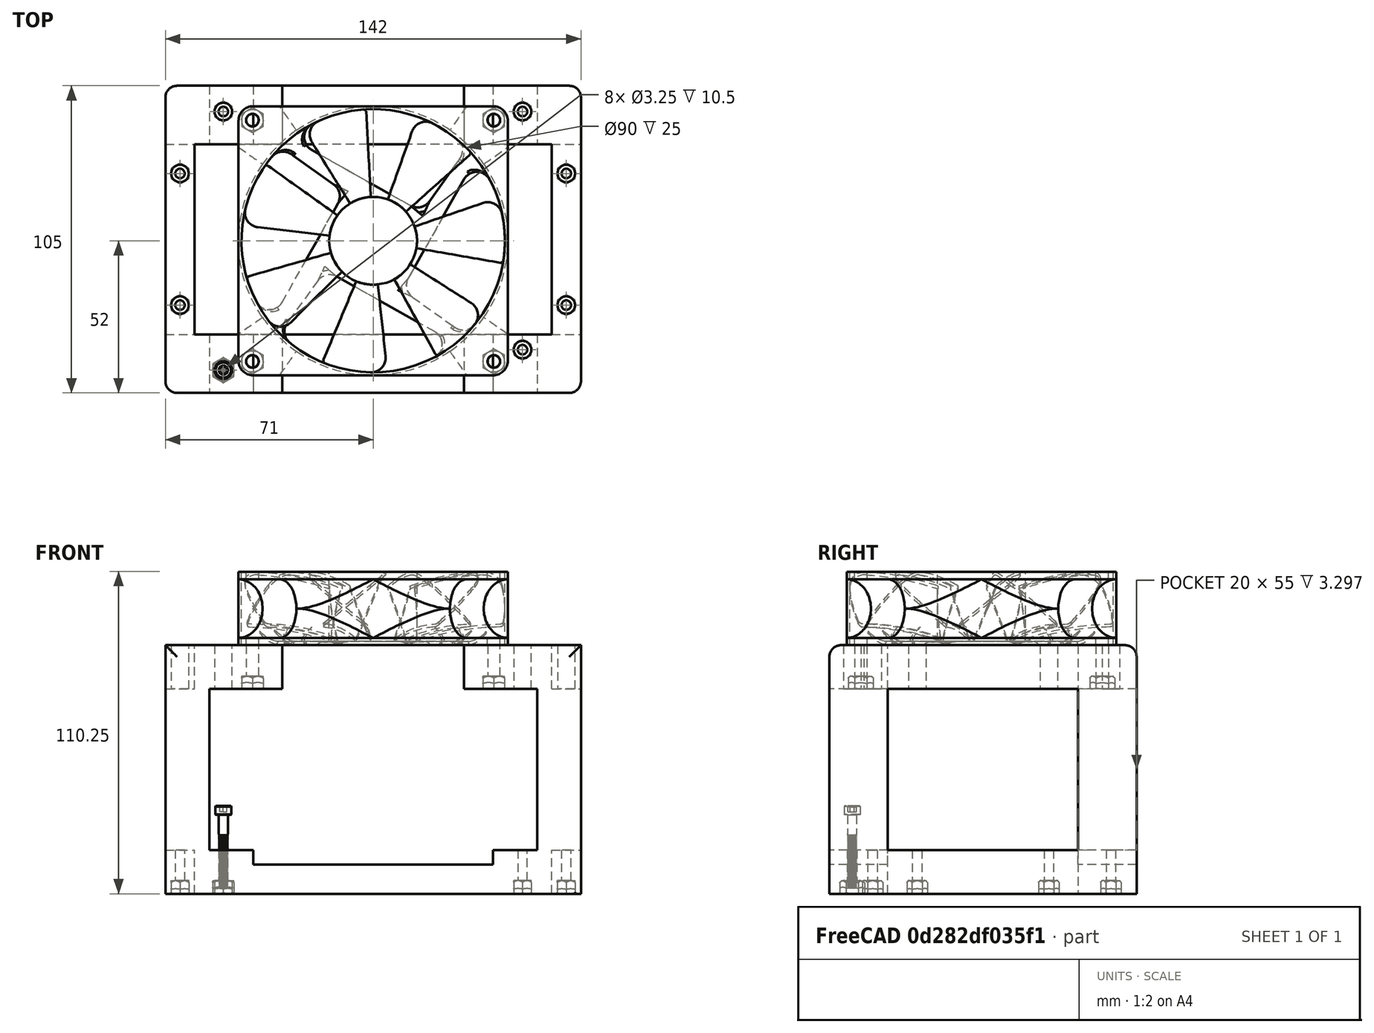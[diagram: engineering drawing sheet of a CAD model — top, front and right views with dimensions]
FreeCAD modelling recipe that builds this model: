
FCSTD DOCUMENT  (FreeCAD 0.20R29410 (Git))
Label: OdroidH4MountV3_2024_07_16
License: All rights reserved
LicenseURL: http://en.wikipedia.org/wiki/All_rights_reserved
objects: Part::MultiFuse×32, Part::FeaturePython×26, Part::Cylinder×13, Sketcher::SketchObject×10, Part::Extrusion×9, Part::Compound×5, Part::Feature×4, Mesh::Feature×1, Part::Cut×1, Part::Fillet×1, App::Part×1
note: 101 computed .brp shape members not serialized (recipe doc carries the construction recipe); baked Part::Feature solids carry a one-line shape summary decoded from their .brp

FEATURE [Mesh::Feature] Odroid_H004  label="Odroid-H004"
  Placement = pos=(16,0,25) rot=(0,0,1;0rad)
FEATURE [Part::Feature] Part__Feature002  label="fan form001"
  shape: bbox 105.3 x 105.3 x 25.46 mm, 118 faces (baked)
FEATURE [Part::Feature] Part__Feature003  label="fan001"
  Placement = pos=(0,0,1.25) rot=(0,0,-1;0.171016rad)
  shape: bbox 91.23 x 90.98 x 28.5 mm, 54 faces (baked)
FEATURE [Part::MultiFuse] Fusion  label="fan002"
  Placement = pos=(71,62,85) rot=(0,0,1;0rad)
  Shapes = -> [Part__Feature002,Part__Feature003]
FEATURE [Sketcher::SketchObject] Sketch006
  FullyConstrained = true
  Placement = pos=(0,0,0) rot=(0.57735,0.57735,0.57735;2.0944rad)
  sketch-geometry (8):
    g0: LineSegment StartX=30 StartY=15 StartZ=0 EndX=95 EndY=15 EndZ=0
    g1: LineSegment StartX=95 StartY=15 StartZ=0 EndX=95 EndY=0 EndZ=0
    g2: LineSegment StartX=95 StartY=0 StartZ=0 EndX=30 EndY=0 EndZ=0
    g3: LineSegment StartX=30 StartY=0 StartZ=0 EndX=30 EndY=15 EndZ=0
    g4: LineSegment StartX=30 StartY=85 StartZ=0 EndX=95 EndY=85 EndZ=0
    g5: LineSegment StartX=95 StartY=85 StartZ=0 EndX=95 EndY=70 EndZ=0
    g6: LineSegment StartX=95 StartY=70 StartZ=0 EndX=30 EndY=70 EndZ=0
    g7: LineSegment StartX=30 StartY=70 StartZ=0 EndX=30 EndY=85 EndZ=0
  constraints (24):
    c: Coincident(g0,g1)
    c: Coincident(g1,g2)
    c: Coincident(g2,g3)
    c: Coincident(g3,g0)
    c: Horizontal(g0)
    c: Horizontal(g2)
    c: Vertical(g1)
    c: Vertical(g3)
    c: PointOnObject(g1,g-1)
    c: Coincident(g4,g5)
    c: Coincident(g5,g6)
    c: Coincident(g6,g7)
    c: Coincident(g7,g4)
    c: Horizontal(g4)
    c: Horizontal(g6)
    c: Vertical(g5)
    c: Vertical(g7)
    c: DistanceX(g2) = 30
    c: DistanceY(g2,g0) = 15
    c: DistanceX(g0,g0) = 65
    c: DistanceY(g6,g4) = 15
    c: Vertical(g5,g0)
    c: Vertical(g6,g0)
    c: DistanceY(g0,g6) = 55
FEATURE [Sketcher::SketchObject] Sketch008
  FullyConstrained = true
  Placement = pos=(0,0,0) rot=(1,0,0;1.5708rad)
  sketch-geometry (16):
    g0: LineSegment StartX=0 StartY=0 StartZ=0 EndX=142 EndY=0 EndZ=0
    g1: LineSegment StartX=142 StartY=0 StartZ=0 EndX=142 EndY=85 EndZ=0
    g2: LineSegment StartX=142 StartY=85 StartZ=0 EndX=102 EndY=85 EndZ=0
    g3: LineSegment StartX=102 StartY=85 StartZ=0 EndX=102 EndY=70 EndZ=0
    g4: LineSegment StartX=102 StartY=70 StartZ=0 EndX=127 EndY=70 EndZ=0
    g5: LineSegment StartX=127 StartY=70 StartZ=0 EndX=127 EndY=15 EndZ=0
    g6: LineSegment StartX=127 StartY=15 StartZ=0 EndX=112 EndY=15 EndZ=0
    g7: LineSegment StartX=112 StartY=15 StartZ=0 EndX=112 EndY=10 EndZ=0
    g8: LineSegment StartX=112 StartY=10 StartZ=0 EndX=30 EndY=10 EndZ=0
    g9: LineSegment StartX=30 StartY=10 StartZ=0 EndX=30 EndY=15 EndZ=0
    g10: LineSegment StartX=30 StartY=15 StartZ=0 EndX=15 EndY=15 EndZ=0
    g11: LineSegment StartX=15 StartY=15 StartZ=0 EndX=15 EndY=70 EndZ=0
    g12: LineSegment StartX=15 StartY=70 StartZ=0 EndX=40 EndY=70 EndZ=0
    g13: LineSegment StartX=40 StartY=70 StartZ=0 EndX=40 EndY=85 EndZ=0
    g14: LineSegment StartX=40 StartY=85 StartZ=0 EndX=0 EndY=85 EndZ=0
    g15: LineSegment StartX=0 StartY=85 StartZ=0 EndX=0 EndY=0 EndZ=0
  constraints (47):
    c: Coincident(g0,g-1)
    c: Horizontal(g0)
    c: Coincident(g1,g0)
    c: Vertical(g1)
    c: Coincident(g2,g1)
    c: Horizontal(g2)
    c: Coincident(g3,g2)
    c: Vertical(g3)
    c: Coincident(g4,g3)
    c: Horizontal(g4)
    c: Coincident(g5,g4)
    c: Vertical(g5)
    c: Coincident(g6,g5)
    c: Horizontal(g6)
    c: Coincident(g7,g6)
    c: Coincident(g8,g7)
    c: Horizontal(g8)
    c: Coincident(g9,g8)
    c: Vertical(g9)
    c: Coincident(g10,g9)
    c: Horizontal(g10)
    c: Coincident(g11,g10)
    c: Vertical(g11)
    c: Coincident(g12,g11)
    c: Horizontal(g12)
    c: Coincident(g13,g12)
    c: Vertical(g13)
    c: Coincident(g14,g13)
    c: Horizontal(g14)
    c: Coincident(g15,g14)
    c: Coincident(g15,g0)
    c: Vertical(g15)
    c: DistanceX(g14,g14) = 40
    c: DistanceY(g0,g14) = 85
    c: DistanceX(g12,g12) = 25
    c: DistanceY(g12,g13) = 15
    c: DistanceY(g11,g11) = 55
    c: DistanceY(g9,g9) = 5
    c: DistanceX(g10,g10) = 15
    c: DistanceX(g8,g8) = 82
    c: DistanceY(g7,g7) = 5
    c: DistanceX(g6,g6) = 15
    c: DistanceY(g5,g5) = 55
    c: DistanceX(g4,g4) = 25
    c: DistanceX(g2,g2) = 40
    c: DistanceY(g3,g3) = 15
    c: DistanceX(g0,g0) = 142
FEATURE [Part::Extrusion] Extrude008
  Base = -> Sketch008
  Dir = (0,-1,-3e-16)
  DirMode = 2
  FaceMakerClass = Part::FaceMakerBullseye
  LengthFwd = 20
  LengthRev = 0
  Placement = pos=(0,30,0) rot=(0,0,1;0rad)
  Solid = true
  Symmetric = false
FEATURE [Sketcher::SketchObject] Sketch009
  FullyConstrained = true
  Placement = pos=(0,0,0) rot=(1,0,0;1.5708rad)
  sketch-geometry (16):
    g0: LineSegment StartX=0 StartY=0 StartZ=0 EndX=142 EndY=0 EndZ=0
    g1: LineSegment StartX=142 StartY=0 StartZ=0 EndX=142 EndY=85 EndZ=0
    g2: LineSegment StartX=142 StartY=85 StartZ=0 EndX=102 EndY=85 EndZ=0
    g3: LineSegment StartX=102 StartY=85 StartZ=0 EndX=102 EndY=70 EndZ=0
    g4: LineSegment StartX=102 StartY=70 StartZ=0 EndX=127 EndY=70 EndZ=0
    g5: LineSegment StartX=127 StartY=70 StartZ=0 EndX=127 EndY=15 EndZ=0
    g6: LineSegment StartX=127 StartY=15 StartZ=0 EndX=112 EndY=15 EndZ=0
    g7: LineSegment StartX=112 StartY=15 StartZ=0 EndX=112 EndY=10 EndZ=0
    g8: LineSegment StartX=112 StartY=10 StartZ=0 EndX=30 EndY=10 EndZ=0
    g9: LineSegment StartX=30 StartY=10 StartZ=0 EndX=30 EndY=15 EndZ=0
    g10: LineSegment StartX=30 StartY=15 StartZ=0 EndX=15 EndY=15 EndZ=0
    g11: LineSegment StartX=15 StartY=15 StartZ=0 EndX=15 EndY=70 EndZ=0
    g12: LineSegment StartX=15 StartY=70 StartZ=0 EndX=40 EndY=70 EndZ=0
    g13: LineSegment StartX=40 StartY=70 StartZ=0 EndX=40 EndY=85 EndZ=0
    g14: LineSegment StartX=40 StartY=85 StartZ=0 EndX=0 EndY=85 EndZ=0
    g15: LineSegment StartX=0 StartY=85 StartZ=0 EndX=0 EndY=0 EndZ=0
  constraints (47):
    c: Coincident(g0,g-1)
    c: Horizontal(g0)
    c: Coincident(g1,g0)
    c: Vertical(g1)
    c: Coincident(g2,g1)
    c: Horizontal(g2)
    c: Coincident(g3,g2)
    c: Vertical(g3)
    c: Coincident(g4,g3)
    c: Horizontal(g4)
    c: Coincident(g5,g4)
    c: Vertical(g5)
    c: Coincident(g6,g5)
    c: Horizontal(g6)
    c: Coincident(g7,g6)
    c: Coincident(g8,g7)
    c: Horizontal(g8)
    c: Coincident(g9,g8)
    c: Vertical(g9)
    c: Coincident(g10,g9)
    c: Horizontal(g10)
    c: Coincident(g11,g10)
    c: Vertical(g11)
    c: Coincident(g12,g11)
    c: Horizontal(g12)
    c: Coincident(g13,g12)
    c: Vertical(g13)
    c: Coincident(g14,g13)
    c: Horizontal(g14)
    c: Coincident(g15,g14)
    c: Coincident(g15,g0)
    c: Vertical(g15)
    c: DistanceX(g14,g14) = 40
    c: DistanceY(g0,g14) = 85
    c: DistanceX(g12,g12) = 25
    c: DistanceY(g12,g13) = 15
    c: DistanceY(g11,g11) = 55
    c: DistanceY(g9,g9) = 5
    c: DistanceX(g10,g10) = 15
    c: DistanceX(g8,g8) = 82
    c: DistanceY(g7,g7) = 5
    c: DistanceX(g6,g6) = 15
    c: DistanceY(g5,g5) = 55
    c: DistanceX(g4,g4) = 25
    c: DistanceX(g2,g2) = 40
    c: DistanceY(g3,g3) = 15
    c: DistanceX(g0,g0) = 142
FEATURE [Part::Extrusion] Extrude009
  Base = -> Sketch009
  Dir = (0,-1,-3e-16)
  DirMode = 2
  FaceMakerClass = Part::FaceMakerBullseye
  LengthFwd = 20
  LengthRev = 0
  Placement = pos=(0,115,0) rot=(0,0,1;0rad)
  Solid = true
  Symmetric = false
FEATURE [Sketcher::SketchObject] Sketch010
  FullyConstrained = true
  Placement = pos=(0,0,0) rot=(0.57735,0.57735,0.57735;2.0944rad)
  sketch-geometry (8):
    g0: LineSegment StartX=30 StartY=15 StartZ=0 EndX=95 EndY=15 EndZ=0
    g1: LineSegment StartX=95 StartY=15 StartZ=0 EndX=95 EndY=0 EndZ=0
    g2: LineSegment StartX=95 StartY=0 StartZ=0 EndX=30 EndY=0 EndZ=0
    g3: LineSegment StartX=30 StartY=0 StartZ=0 EndX=30 EndY=15 EndZ=0
    g4: LineSegment StartX=30 StartY=85 StartZ=0 EndX=95 EndY=85 EndZ=0
    g5: LineSegment StartX=95 StartY=85 StartZ=0 EndX=95 EndY=70 EndZ=0
    g6: LineSegment StartX=95 StartY=70 StartZ=0 EndX=30 EndY=70 EndZ=0
    g7: LineSegment StartX=30 StartY=70 StartZ=0 EndX=30 EndY=85 EndZ=0
  constraints (24):
    c: Coincident(g0,g1)
    c: Coincident(g1,g2)
    c: Coincident(g2,g3)
    c: Coincident(g3,g0)
    c: Horizontal(g0)
    c: Horizontal(g2)
    c: Vertical(g1)
    c: Vertical(g3)
    c: PointOnObject(g1,g-1)
    c: Coincident(g4,g5)
    c: Coincident(g5,g6)
    c: Coincident(g6,g7)
    c: Coincident(g7,g4)
    c: Horizontal(g4)
    c: Horizontal(g6)
    c: Vertical(g5)
    c: Vertical(g7)
    c: DistanceX(g2) = 30
    c: DistanceY(g2,g0) = 15
    c: DistanceX(g0,g0) = 65
    c: DistanceY(g6,g4) = 15
    c: Vertical(g5,g0)
    c: Vertical(g6,g0)
    c: DistanceY(g0,g6) = 55
FEATURE [Part::Extrusion] Extrude010
  Base = -> Sketch010
  Dir = (1,0,0)
  DirMode = 2
  FaceMakerClass = Part::FaceMakerBullseye
  LengthFwd = 10
  LengthRev = 0
  Solid = true
  Symmetric = false
FEATURE [Sketcher::SketchObject] Sketch011
  FullyConstrained = true
  Placement = pos=(0,0,0) rot=(0.57735,0.57735,0.57735;2.0944rad)
  sketch-geometry (8):
    g0: LineSegment StartX=30 StartY=15 StartZ=0 EndX=95 EndY=15 EndZ=0
    g1: LineSegment StartX=95 StartY=15 StartZ=0 EndX=95 EndY=0 EndZ=0
    g2: LineSegment StartX=95 StartY=0 StartZ=0 EndX=30 EndY=0 EndZ=0
    g3: LineSegment StartX=30 StartY=0 StartZ=0 EndX=30 EndY=15 EndZ=0
    g4: LineSegment StartX=30 StartY=85 StartZ=0 EndX=95 EndY=85 EndZ=0
    g5: LineSegment StartX=95 StartY=85 StartZ=0 EndX=95 EndY=70 EndZ=0
    g6: LineSegment StartX=95 StartY=70 StartZ=0 EndX=30 EndY=70 EndZ=0
    g7: LineSegment StartX=30 StartY=70 StartZ=0 EndX=30 EndY=85 EndZ=0
  constraints (24):
    c: Coincident(g0,g1)
    c: Coincident(g1,g2)
    c: Coincident(g2,g3)
    c: Coincident(g3,g0)
    c: Horizontal(g0)
    c: Horizontal(g2)
    c: Vertical(g1)
    c: Vertical(g3)
    c: PointOnObject(g1,g-1)
    c: Coincident(g4,g5)
    c: Coincident(g5,g6)
    c: Coincident(g6,g7)
    c: Coincident(g7,g4)
    c: Horizontal(g4)
    c: Horizontal(g6)
    c: Vertical(g5)
    c: Vertical(g7)
    c: DistanceX(g2) = 30
    c: DistanceY(g2,g0) = 15
    c: DistanceX(g0,g0) = 65
    c: DistanceY(g6,g4) = 15
    c: Vertical(g5,g0)
    c: Vertical(g6,g0)
    c: DistanceY(g0,g6) = 55
FEATURE [Part::Extrusion] Extrude011
  Base = -> Sketch011
  Dir = (1,0,0)
  DirMode = 2
  FaceMakerClass = Part::FaceMakerBullseye
  LengthFwd = 10
  LengthRev = 0
  Placement = pos=(132,0,0) rot=(0,0,1;0rad)
  Solid = true
  Symmetric = false
FEATURE [Part::MultiFuse] Fusion002
  Shapes = -> [Extrude011,Extrude008,Extrude009,Extrude010]
FEATURE [Sketcher::SketchObject] Sketch
  FullyConstrained = true
  sketch-geometry (4):
    g0: Circle CenterX=19.81 CenterY=106.19 CenterZ=0 NormalX=0 NormalY=0 NormalZ=1 AngleXU=0 Radius=1.625
    g1: Circle CenterX=122.04 CenterY=106.19 CenterZ=0 NormalX=0 NormalY=0 NormalZ=1 AngleXU=0 Radius=1.625
    g2: Circle CenterX=19.81 CenterY=17.78 CenterZ=0 NormalX=0 NormalY=0 NormalZ=1 AngleXU=0 Radius=1.625
    g3: Circle CenterX=122.04 CenterY=24.77 CenterZ=0 NormalX=0 NormalY=0 NormalZ=1 AngleXU=0 Radius=1.625
  constraints (12):
    c: Vertical(g0,g2)
    c: DistanceY(g2,g0) = 88.41
    c: DistanceX(g2) = 19.81
    c: DistanceY(g2) = 17.78
    c: DistanceX(g2,g3) = 102.23
    c: DistanceY(g2,g3) = 6.99
    c: DistanceX(g1,g3) = 0
    c: DistanceY(g0,g1) = 0
    c: Equal(g2,g3)
    c: Equal(g2,g1)
    c: Equal(g2,g0)
    c: Diameter(g2) = 3.25
FEATURE [Sketcher::SketchObject] Sketch012
  FullyConstrained = true
  sketch-geometry (4):
    g0: Circle CenterX=29.75 CenterY=103.25 CenterZ=0 NormalX=0 NormalY=0 NormalZ=1 AngleXU=0 Radius=2.125
    g1: Circle CenterX=112.25 CenterY=103.25 CenterZ=0 NormalX=0 NormalY=0 NormalZ=1 AngleXU=0 Radius=2.125
    g2: Circle CenterX=29.75 CenterY=20.75 CenterZ=0 NormalX=0 NormalY=0 NormalZ=1 AngleXU=0 Radius=2.125
    g3: Circle CenterX=112.25 CenterY=20.75 CenterZ=0 NormalX=0 NormalY=0 NormalZ=1 AngleXU=0 Radius=2.125
  constraints (12):
    c: Vertical(g0,g2)
    c: DistanceX(g1,g3) = 0
    c: DistanceY(g0,g1) = 0
    c: Equal(g2,g3)
    c: Equal(g2,g1)
    c: Equal(g2,g0)
    c: Diameter(g2) = 4.25
    c: DistanceX(g2) = 29.75
    c: DistanceY(g2) = 20.75
    c: Horizontal(g3,g2)
    c: DistanceX(g2,g3) = 82.5
    c: DistanceY(g2,g0) = 82.5
FEATURE [Part::Extrusion] Extrude
  Base = -> Sketch
  Dir = (0,0,1)
  DirMode = 2
  FaceMakerClass = Part::FaceMakerBullseye
  LengthFwd = 15
  LengthRev = 0
  Solid = true
  Symmetric = false
FEATURE [Part::Extrusion] Extrude012
  Base = -> Sketch012
  Dir = (0,0,1)
  DirMode = 2
  FaceMakerClass = Part::FaceMakerBullseye
  LengthFwd = 15
  LengthRev = 0
  Placement = pos=(0,0,70) rot=(0,0,1;0rad)
  Solid = true
  Symmetric = false
FEATURE [Sketcher::SketchObject] Sketch013
  FullyConstrained = true
  sketch-geometry (4):
    g0: Circle CenterX=19.81 CenterY=106.19 CenterZ=0 NormalX=0 NormalY=0 NormalZ=1 AngleXU=0 Radius=3
    g1: Circle CenterX=122.04 CenterY=106.19 CenterZ=0 NormalX=0 NormalY=0 NormalZ=1 AngleXU=0 Radius=3
    g2: Circle CenterX=19.81 CenterY=17.78 CenterZ=0 NormalX=0 NormalY=0 NormalZ=1 AngleXU=0 Radius=3
    g3: Circle CenterX=122.04 CenterY=24.77 CenterZ=0 NormalX=0 NormalY=0 NormalZ=1 AngleXU=0 Radius=3
  constraints (12):
    c: Vertical(g0,g2)
    c: DistanceY(g2,g0) = 88.41
    c: DistanceX(g2) = 19.81
    c: DistanceY(g2) = 17.78
    c: DistanceX(g2,g3) = 102.23
    c: DistanceY(g2,g3) = 6.99
    c: DistanceX(g1,g3) = 0
    c: DistanceY(g0,g1) = 0
    c: Equal(g2,g3)
    c: Equal(g2,g1)
    c: Equal(g2,g0)
    c: Diameter(g2) = 6
FEATURE [Part::Extrusion] Extrude013
  Base = -> Sketch013
  Dir = (0,0,1)
  DirMode = 2
  FaceMakerClass = Part::FaceMakerBullseye
  LengthFwd = 15
  LengthRev = 0
  Placement = pos=(0,0,70) rot=(0,0,1;0rad)
  Solid = true
  Symmetric = false
FEATURE [Sketcher::SketchObject] Sketch014
  FullyConstrained = true
  sketch-geometry (4):
    g0: Circle CenterX=5 CenterY=85 CenterZ=0 NormalX=0 NormalY=0 NormalZ=1 AngleXU=0 Radius=1.625
    g1: Circle CenterX=137 CenterY=85 CenterZ=0 NormalX=0 NormalY=0 NormalZ=1 AngleXU=0 Radius=1.625
    g2: Circle CenterX=5 CenterY=40 CenterZ=0 NormalX=0 NormalY=0 NormalZ=1 AngleXU=0 Radius=1.625
    g3: Circle CenterX=137 CenterY=40 CenterZ=0 NormalX=0 NormalY=0 NormalZ=1 AngleXU=0 Radius=1.625
  constraints (12):
    c: Vertical(g0,g2)
    c: DistanceY(g2,g0) = 45
    c: DistanceX(g2,g3) = 132
    c: DistanceY(g2,g3) = 0
    c: DistanceX(g1,g3) = 0
    c: DistanceY(g0,g1) = 0
    c: Equal(g2,g3)
    c: Equal(g2,g1)
    c: Equal(g2,g0)
    c: Diameter(g2) = 3.25
    c: DistanceX(g2) = 5
    c: DistanceY(g2) = 40
FEATURE [Sketcher::SketchObject] Sketch015
  FullyConstrained = true
  sketch-geometry (4):
    g0: Circle CenterX=5 CenterY=85 CenterZ=0 NormalX=0 NormalY=0 NormalZ=1 AngleXU=0 Radius=3
    g1: Circle CenterX=137 CenterY=85 CenterZ=0 NormalX=0 NormalY=0 NormalZ=1 AngleXU=0 Radius=3
    g2: Circle CenterX=5 CenterY=40 CenterZ=0 NormalX=0 NormalY=0 NormalZ=1 AngleXU=0 Radius=3
    g3: Circle CenterX=137 CenterY=40 CenterZ=0 NormalX=0 NormalY=0 NormalZ=1 AngleXU=0 Radius=3
  constraints (12):
    c: Vertical(g0,g2)
    c: DistanceY(g2,g0) = 45
    c: DistanceX(g2,g3) = 132
    c: DistanceY(g2,g3) = 0
    c: DistanceX(g1,g3) = 0
    c: DistanceY(g0,g1) = 0
    c: Equal(g2,g3)
    c: Equal(g2,g1)
    c: Equal(g2,g0)
    c: Diameter(g2) = 6
    c: DistanceX(g2) = 5
    c: DistanceY(g2) = 40
FEATURE [Part::Extrusion] Extrude014
  Base = -> Sketch014
  Dir = (0,0,1)
  DirMode = 2
  FaceMakerClass = Part::FaceMakerBullseye
  LengthFwd = 15
  LengthRev = 0
  Solid = true
  Symmetric = false
FEATURE [Part::Extrusion] Extrude015
  Base = -> Sketch015
  Dir = (0,0,1)
  DirMode = 2
  FaceMakerClass = Part::FaceMakerBullseye
  LengthFwd = 15
  LengthRev = 0
  Placement = pos=(0,0,70) rot=(0,0,1;0rad)
  Solid = true
  Symmetric = false
FEATURE [Part::FeaturePython] Clone009  label="M4Nut002"  # WARN: FeaturePython — macro-defined, semantics opaque (R4)
  AttacherType = Attacher::AttachEngine3D
  Fuse = false
  Placement = pos=(0,0,1.1) rot=(1,0,0;0rad)
  Scale = (1.05,1.05,1)
FEATURE [Part::Cylinder] Cylinder
  Angle = 360
  AttacherType = Attacher::AttachEngine3D
  FirstAngle = 0
  Height = 4.4
  Radius = 3
  SecondAngle = 0
FEATURE [Part::Feature] Part__Feature264  label="M4Nut"
  Placement = pos=(19.81,17.78,2) rot=(1,0,0;0rad)
  shape: bbox 8.084 x 8.084 x 2.714 mm, 34 faces (baked)
FEATURE [Part::FeaturePython] Clone  label="M4Nut001"  # Draft clone (typed FeaturePython)
  AttacherType = Attacher::AttachEngine3D
  Fuse = false
  Objects = -> [Part__Feature264]
  Placement = pos=(0,0,2.2) rot=(1,0,0;0rad)
  Scale = (1.05,1.05,2)
FEATURE [Part::Compound] Compound
  Links = -> [Clone]
FEATURE [Part::MultiFuse] Fusion003  label="m4NutCut001"
  Shapes = -> [Cylinder,Compound]
FEATURE [Part::MultiFuse] Fusion009  label="M4NutCut"
  Placement = pos=(19.81,17.78,0) rot=(0,0,1;0rad)
  Shapes = -> [Clone009,Fusion003]
FEATURE [Part::Feature] Part__Feature  label="m3x30"
  Placement = pos=(19.81,17.78,16) rot=(0,0,1;0rad)
  shape: bbox 5.501 x 5.501 x 28.29 mm, 108 faces (baked)
FEATURE [Part::FeaturePython] Clone010  label="M4Nut003"  # WARN: FeaturePython — macro-defined, semantics opaque (R4)
  AttacherType = Attacher::AttachEngine3D
  Fuse = false
  Placement = pos=(0,0,2.2) rot=(1,0,0;0rad)
  Scale = (1.05,1.05,2)
FEATURE [Part::FeaturePython] Clone011  label="M4Nut004"  # WARN: FeaturePython — macro-defined, semantics opaque (R4)
  AttacherType = Attacher::AttachEngine3D
  Fuse = false
  Placement = pos=(0,0,1.1) rot=(1,0,0;0rad)
  Scale = (1.05,1.05,1)
FEATURE [Part::Compound] Compound001
  Links = -> [Clone010]
FEATURE [Part::Cylinder] Cylinder001
  Angle = 360
  AttacherType = Attacher::AttachEngine3D
  FirstAngle = 0
  Height = 4.4
  Radius = 3
  SecondAngle = 0
FEATURE [Part::MultiFuse] Fusion010  label="m4NutCut002"
  Shapes = -> [Cylinder001,Compound001]
FEATURE [Part::MultiFuse] Fusion011  label="M4NutCut001"
  Placement = pos=(29.75,20.75,70) rot=(0,0,1;0rad)
  Shapes = -> [Clone011,Fusion010]
FEATURE [Part::FeaturePython] Clone001  label="M3Nut001"  # WARN: FeaturePython — macro-defined, semantics opaque (R4)
  AttacherType = Attacher::AttachEngine3D
  Fuse = false
  Placement = pos=(0,0,2.25) rot=(0,0,1;0rad)
  Scale = (1.1,1.1,2.5)
FEATURE [Part::FeaturePython] Clone002  label="M3Nut002"  # WARN: FeaturePython — macro-defined, semantics opaque (R4)
  AttacherType = Attacher::AttachEngine3D
  Fuse = false
  Placement = pos=(0,0,0.9) rot=(0,0,1;0rad)
  Scale = (1.1,1.1,1)
FEATURE [Part::Cylinder] Cylinder005
  Angle = 360
  AttacherType = Attacher::AttachEngine3D
  FirstAngle = 0
  Height = 4.5
  Radius = 2
  SecondAngle = 0
FEATURE [Part::MultiFuse] Fusion018
  Shapes = -> [Clone001,Cylinder005]
FEATURE [Part::MultiFuse] Fusion019  label="m3NutCut001"
  Placement = pos=(19.81,17.78,0) rot=(0,0,1;0rad)
  Shapes = -> [Clone002,Fusion018]
FEATURE [Part::FeaturePython] Clone018  label="M3Nut003"  # WARN: FeaturePython — macro-defined, semantics opaque (R4)
  AttacherType = Attacher::AttachEngine3D
  Fuse = false
  Placement = pos=(0,0,2.25) rot=(0,0,1;0rad)
  Scale = (1.1,1.1,2.5)
FEATURE [Part::FeaturePython] Clone019  label="M3Nut004"  # WARN: FeaturePython — macro-defined, semantics opaque (R4)
  AttacherType = Attacher::AttachEngine3D
  Fuse = false
  Placement = pos=(0,0,0.9) rot=(0,0,1;0rad)
  Scale = (1.1,1.1,1)
FEATURE [Part::Cylinder] Cylinder006
  Angle = 360
  AttacherType = Attacher::AttachEngine3D
  FirstAngle = 0
  Height = 4.5
  Radius = 2
  SecondAngle = 0
FEATURE [Part::MultiFuse] Fusion020
  Shapes = -> [Clone018,Cylinder006]
FEATURE [Part::MultiFuse] Fusion021  label="m3NutCut002"
  Placement = pos=(122.04,24.77,0) rot=(0,0,1;0rad)
  Shapes = -> [Clone019,Fusion020]
FEATURE [Part::FeaturePython] Clone020  label="M3Nut005"  # WARN: FeaturePython — macro-defined, semantics opaque (R4)
  AttacherType = Attacher::AttachEngine3D
  Fuse = false
  Placement = pos=(0,0,2.25) rot=(0,0,1;0rad)
  Scale = (1.1,1.1,2.5)
FEATURE [Part::FeaturePython] Clone021  label="M3Nut006"  # WARN: FeaturePython — macro-defined, semantics opaque (R4)
  AttacherType = Attacher::AttachEngine3D
  Fuse = false
  Placement = pos=(0,0,0.9) rot=(0,0,1;0rad)
  Scale = (1.1,1.1,1)
FEATURE [Part::Cylinder] Cylinder007
  Angle = 360
  AttacherType = Attacher::AttachEngine3D
  FirstAngle = 0
  Height = 4.5
  Radius = 2
  SecondAngle = 0
FEATURE [Part::MultiFuse] Fusion022
  Shapes = -> [Clone020,Cylinder007]
FEATURE [Part::MultiFuse] Fusion023  label="m3NutCut003"
  Placement = pos=(19.81,106.19,0) rot=(0,0,1;0rad)
  Shapes = -> [Clone021,Fusion022]
FEATURE [Part::FeaturePython] Clone022  label="M3Nut007"  # WARN: FeaturePython — macro-defined, semantics opaque (R4)
  AttacherType = Attacher::AttachEngine3D
  Fuse = false
  Placement = pos=(0,0,2.25) rot=(0,0,1;0rad)
  Scale = (1.1,1.1,2.5)
FEATURE [Part::FeaturePython] Clone023  label="M3Nut008"  # WARN: FeaturePython — macro-defined, semantics opaque (R4)
  AttacherType = Attacher::AttachEngine3D
  Fuse = false
  Placement = pos=(0,0,0.9) rot=(0,0,1;0rad)
  Scale = (1.1,1.1,1)
FEATURE [Part::Cylinder] Cylinder008
  Angle = 360
  AttacherType = Attacher::AttachEngine3D
  FirstAngle = 0
  Height = 4.5
  Radius = 2
  SecondAngle = 0
FEATURE [Part::MultiFuse] Fusion024
  Shapes = -> [Clone022,Cylinder008]
FEATURE [Part::MultiFuse] Fusion025  label="m3NutCut004"
  Placement = pos=(122.04,106.19,0) rot=(0,0,1;0rad)
  Shapes = -> [Clone023,Fusion024]
FEATURE [Part::MultiFuse] Fusion026
  Shapes = -> [Fusion019,Fusion021,Fusion023,Fusion025]
FEATURE [Part::FeaturePython] Clone024  label="M4Nut005"  # WARN: FeaturePython — macro-defined, semantics opaque (R4)
  AttacherType = Attacher::AttachEngine3D
  Fuse = false
  Placement = pos=(0,0,2.2) rot=(1,0,0;0rad)
  Scale = (1.05,1.05,2)
FEATURE [Part::FeaturePython] Clone025  label="M4Nut006"  # WARN: FeaturePython — macro-defined, semantics opaque (R4)
  AttacherType = Attacher::AttachEngine3D
  Fuse = false
  Placement = pos=(0,0,1.1) rot=(1,0,0;0rad)
  Scale = (1.05,1.05,1)
FEATURE [Part::Compound] Compound002
  Links = -> [Clone024]
FEATURE [Part::Cylinder] Cylinder009
  Angle = 360
  AttacherType = Attacher::AttachEngine3D
  FirstAngle = 0
  Height = 4.4
  Radius = 3
  SecondAngle = 0
FEATURE [Part::MultiFuse] Fusion027  label="m4NutCut003"
  Shapes = -> [Cylinder009,Compound002]
FEATURE [Part::MultiFuse] Fusion028  label="M4NutCut002"
  Placement = pos=(112.25,20.75,70) rot=(0,0,1;0rad)
  Shapes = -> [Clone025,Fusion027]
FEATURE [Part::FeaturePython] Clone026  label="M4Nut007"  # WARN: FeaturePython — macro-defined, semantics opaque (R4)
  AttacherType = Attacher::AttachEngine3D
  Fuse = false
  Placement = pos=(0,0,2.2) rot=(1,0,0;0rad)
  Scale = (1.05,1.05,2)
FEATURE [Part::FeaturePython] Clone027  label="M4Nut008"  # WARN: FeaturePython — macro-defined, semantics opaque (R4)
  AttacherType = Attacher::AttachEngine3D
  Fuse = false
  Placement = pos=(0,0,1.1) rot=(1,0,0;0rad)
  Scale = (1.05,1.05,1)
FEATURE [Part::Compound] Compound003
  Links = -> [Clone026]
FEATURE [Part::Cylinder] Cylinder010
  Angle = 360
  AttacherType = Attacher::AttachEngine3D
  FirstAngle = 0
  Height = 4.4
  Radius = 3
  SecondAngle = 0
FEATURE [Part::MultiFuse] Fusion029  label="m4NutCut004"
  Shapes = -> [Cylinder010,Compound003]
FEATURE [Part::MultiFuse] Fusion030  label="M4NutCut003"
  Placement = pos=(29.75,103.25,70) rot=(0,0,1;0rad)
  Shapes = -> [Clone027,Fusion029]
FEATURE [Part::FeaturePython] Clone028  label="M4Nut009"  # WARN: FeaturePython — macro-defined, semantics opaque (R4)
  AttacherType = Attacher::AttachEngine3D
  Fuse = false
  Placement = pos=(0,0,2.2) rot=(1,0,0;0rad)
  Scale = (1.05,1.05,2)
FEATURE [Part::FeaturePython] Clone029  label="M4Nut010"  # WARN: FeaturePython — macro-defined, semantics opaque (R4)
  AttacherType = Attacher::AttachEngine3D
  Fuse = false
  Placement = pos=(0,0,1.1) rot=(1,0,0;0rad)
  Scale = (1.05,1.05,1)
FEATURE [Part::Compound] Compound004
  Links = -> [Clone028]
FEATURE [Part::Cylinder] Cylinder011
  Angle = 360
  AttacherType = Attacher::AttachEngine3D
  FirstAngle = 0
  Height = 4.4
  Radius = 3
  SecondAngle = 0
FEATURE [Part::MultiFuse] Fusion031  label="m4NutCut005"
  Shapes = -> [Cylinder011,Compound004]
FEATURE [Part::MultiFuse] Fusion032  label="M4NutCut004"
  Placement = pos=(112.25,103.25,70) rot=(0,0,1;0rad)
  Shapes = -> [Clone029,Fusion031]
FEATURE [Part::MultiFuse] Fusion033
  Shapes = -> [Fusion011,Fusion028,Fusion032,Fusion030]
FEATURE [Part::MultiFuse] Fusion034
  Shapes = -> [Fusion026,Fusion033]
FEATURE [Part::FeaturePython] Clone030  label="M3Nut009"  # WARN: FeaturePython — macro-defined, semantics opaque (R4)
  AttacherType = Attacher::AttachEngine3D
  Fuse = false
  Placement = pos=(0,0,2.25) rot=(0,0,1;0rad)
  Scale = (1.1,1.1,2.5)
FEATURE [Part::FeaturePython] Clone031  label="M3Nut010"  # WARN: FeaturePython — macro-defined, semantics opaque (R4)
  AttacherType = Attacher::AttachEngine3D
  Fuse = false
  Placement = pos=(0,0,0.9) rot=(0,0,1;0rad)
  Scale = (1.1,1.1,1)
FEATURE [Part::Cylinder] Cylinder012
  Angle = 360
  AttacherType = Attacher::AttachEngine3D
  FirstAngle = 0
  Height = 4.5
  Radius = 2
  SecondAngle = 0
FEATURE [Part::MultiFuse] Fusion035
  Shapes = -> [Clone030,Cylinder012]
FEATURE [Part::MultiFuse] Fusion036  label="m3NutCut005"
  Placement = pos=(5,40,0) rot=(0,0,1;0rad)
  Shapes = -> [Clone031,Fusion035]
FEATURE [Part::FeaturePython] Clone032  label="M3Nut011"  # WARN: FeaturePython — macro-defined, semantics opaque (R4)
  AttacherType = Attacher::AttachEngine3D
  Fuse = false
  Placement = pos=(0,0,2.25) rot=(0,0,1;0rad)
  Scale = (1.1,1.1,2.5)
FEATURE [Part::FeaturePython] Clone033  label="M3Nut012"  # WARN: FeaturePython — macro-defined, semantics opaque (R4)
  AttacherType = Attacher::AttachEngine3D
  Fuse = false
  Placement = pos=(0,0,0.9) rot=(0,0,1;0rad)
  Scale = (1.1,1.1,1)
FEATURE [Part::Cylinder] Cylinder013
  Angle = 360
  AttacherType = Attacher::AttachEngine3D
  FirstAngle = 0
  Height = 4.5
  Radius = 2
  SecondAngle = 0
FEATURE [Part::MultiFuse] Fusion037
  Shapes = -> [Clone032,Cylinder013]
FEATURE [Part::MultiFuse] Fusion038  label="m3NutCut006"
  Placement = pos=(5,85,0) rot=(0,0,1;0rad)
  Shapes = -> [Clone033,Fusion037]
FEATURE [Part::FeaturePython] Clone034  label="M3Nut013"  # WARN: FeaturePython — macro-defined, semantics opaque (R4)
  AttacherType = Attacher::AttachEngine3D
  Fuse = false
  Placement = pos=(0,0,2.25) rot=(0,0,1;0rad)
  Scale = (1.1,1.1,2.5)
FEATURE [Part::FeaturePython] Clone035  label="M3Nut014"  # WARN: FeaturePython — macro-defined, semantics opaque (R4)
  AttacherType = Attacher::AttachEngine3D
  Fuse = false
  Placement = pos=(0,0,0.9) rot=(0,0,1;0rad)
  Scale = (1.1,1.1,1)
FEATURE [Part::Cylinder] Cylinder014
  Angle = 360
  AttacherType = Attacher::AttachEngine3D
  FirstAngle = 0
  Height = 4.5
  Radius = 2
  SecondAngle = 0
FEATURE [Part::MultiFuse] Fusion039
  Shapes = -> [Clone034,Cylinder014]
FEATURE [Part::MultiFuse] Fusion040  label="m3NutCut007"
  Placement = pos=(137,85,0) rot=(0,0,1;0rad)
  Shapes = -> [Clone035,Fusion039]
FEATURE [Part::FeaturePython] Clone036  label="M3Nut015"  # WARN: FeaturePython — macro-defined, semantics opaque (R4)
  AttacherType = Attacher::AttachEngine3D
  Fuse = false
  Placement = pos=(0,0,2.25) rot=(0,0,1;0rad)
  Scale = (1.1,1.1,2.5)
FEATURE [Part::FeaturePython] Clone037  label="M3Nut016"  # WARN: FeaturePython — macro-defined, semantics opaque (R4)
  AttacherType = Attacher::AttachEngine3D
  Fuse = false
  Placement = pos=(0,0,0.9) rot=(0,0,1;0rad)
  Scale = (1.1,1.1,1)
FEATURE [Part::Cylinder] Cylinder015
  Angle = 360
  AttacherType = Attacher::AttachEngine3D
  FirstAngle = 0
  Height = 4.5
  Radius = 2
  SecondAngle = 0
FEATURE [Part::MultiFuse] Fusion041
  Shapes = -> [Clone036,Cylinder015]
FEATURE [Part::MultiFuse] Fusion042  label="m3NutCut008"
  Placement = pos=(137,40,0) rot=(0,0,1;0rad)
  Shapes = -> [Clone037,Fusion041]
FEATURE [Part::MultiFuse] Fusion043
  Shapes = -> [Fusion042,Fusion036,Fusion038,Fusion040,Fusion034,Fusion009,Extrude015,Extrude014,Extrude013,Extrude012,Extrude]
FEATURE [Part::Cut] Cut
  Base = -> Fusion002
  Tool = -> Fusion043
FEATURE [Part::Fillet] Fillet
  Base = -> Cut
  Edges = 8 edges r=4: [Edge23,Edge39,Edge40,Edge52,Edge290,Edge292,Edge293,Edge305]
FEATURE [App::Part] Part
  Group = -> [Sketch006,Part__Feature002,Part__Feature003,Fusion,Odroid_H004,Sketch015,Extrude015,Extrude013,Sketch013,Clone,Clone028,Fusion032,Clone029,Compound004,Cylinder011,Fusion031,Clone018,Cylinder012,Clone009,Compound,Cylinder,Clone019,Clone022,Clone024,Fusion033,Fusion018,Clone031,Fusion034,Compound002,Cylinder008,Fusion021,Fusion003,Clone025,Clone035,Clone037,Fusion027,Fusion028,Clone036,Clone032,+61 more]
  Origin = -> Origin
